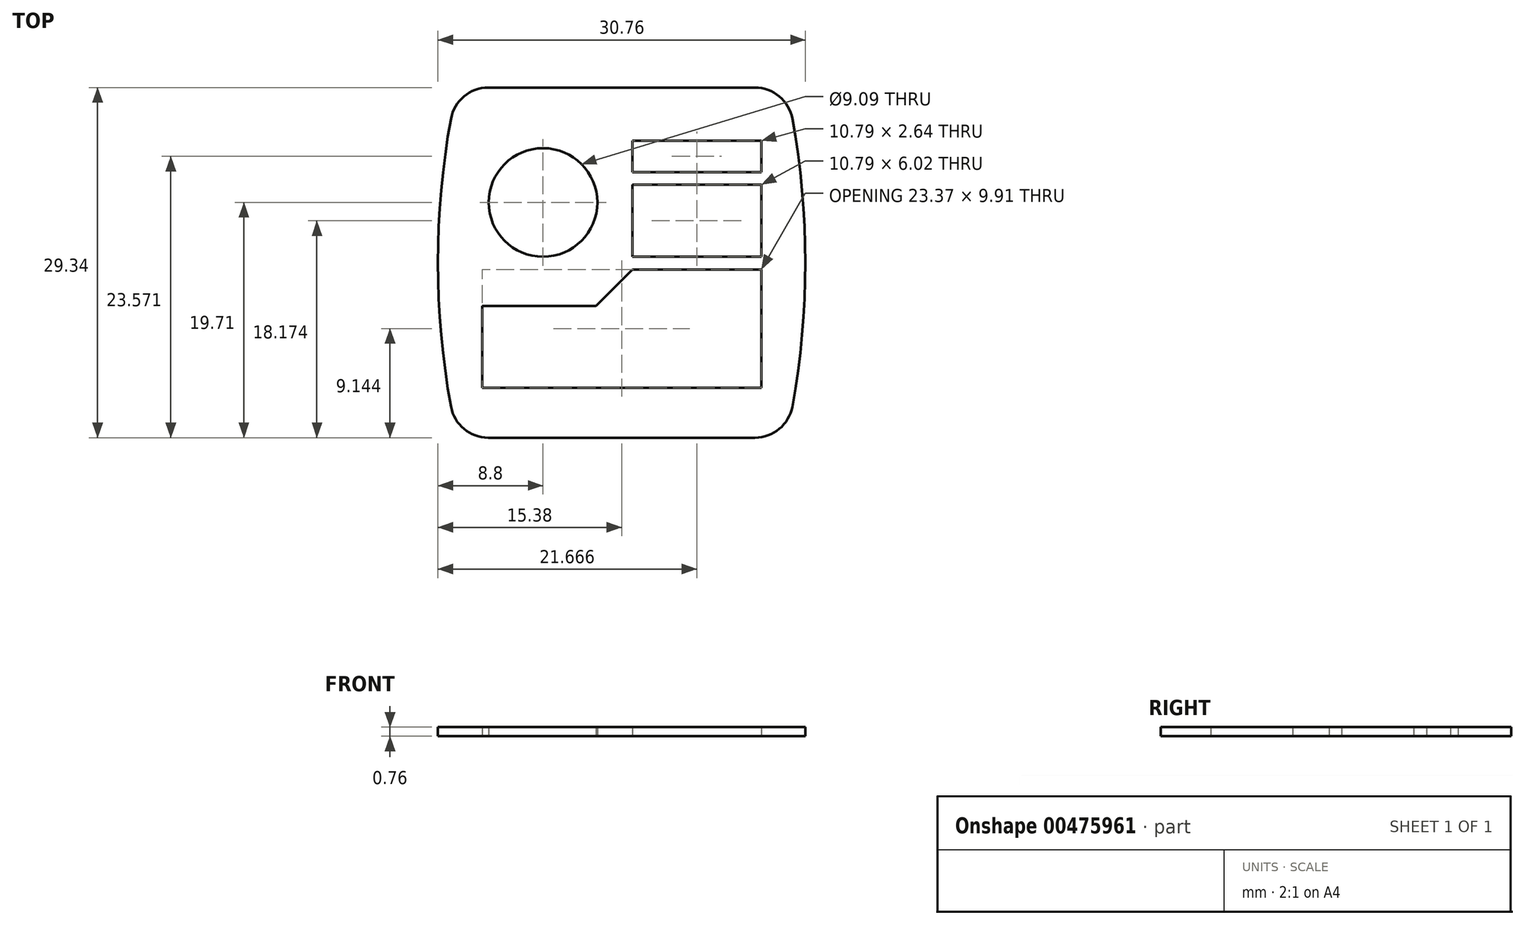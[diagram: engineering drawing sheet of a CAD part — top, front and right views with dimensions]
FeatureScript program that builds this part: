
annotation { "Feature Type Name" : "Feature", "Feature Type Description" : "" }
export const myFeature = defineFeature(function(context is Context, id is Id, definition is map)
    precondition{}
    {
        {
            var Q0;
            Q0=qCreatedBy(makeId("Top.planeOp"),FACE);
            var sketch = newSketch(context, id + "F0", { "sketchPlane" : qUnion([Q0])});
            skLineSegment(sketch, "E0.bottom", {"start": v(-11.16, 0) * mm, "end": v(11.16, 0) * mm});
            skLineSegment(sketch, "E0.top", {"start": v(-11.16, 29.34) * mm, "end": v(11.16, 29.34) * mm});
            skLineSegment(sketch, "E0.left", {"start": v(-13.76, 0) * mm, "end": v(-13.76, 29.34) * mm, "construction": true});
            skLineSegment(sketch, "E0.right", {"start": v(13.76, 0) * mm, "end": v(13.76, 29.34) * mm, "construction": true});
            skArc(sketch, "E1", {"start": v(-14.29, 26.73) * mm, "mid": v(-15.38, 14.67) * mm, "end": v(-14.29, 2.6) * mm});
            skArc(sketch, "E2.MirrorCS", {"start": v(14.29, 26.73) * mm, "mid": v(15.38, 14.67) * mm, "end": v(14.29, 2.6) * mm});
            skPoint(sketch, "E3", {"position": v(-15.38, 14.67) * mm});
            skPoint(sketch, "E4", {"position": v(15.38, 14.67) * mm});
            skCircle(sketch, "E5", {"center": v(-6.58, 19.71) * mm, "radius": 4.55 * mm});
            skLineSegment(sketch, "E6.bottom", {"start": v(0.89, 24.9) * mm, "end": v(11.68, 24.9) * mm});
            skLineSegment(sketch, "E6.top", {"start": v(0.89, 22.25) * mm, "end": v(11.68, 22.25) * mm});
            skLineSegment(sketch, "E6.left", {"start": v(0.89, 24.9) * mm, "end": v(0.89, 22.25) * mm});
            skLineSegment(sketch, "E6.right", {"start": v(11.68, 24.9) * mm, "end": v(11.68, 22.25) * mm});
            skLineSegment(sketch, "E7.bottom", {"start": v(0.89, 21.18) * mm, "end": v(11.68, 21.18) * mm});
            skLineSegment(sketch, "E7.top", {"start": v(0.89, 15.16) * mm, "end": v(11.68, 15.16) * mm});
            skLineSegment(sketch, "E7.left", {"start": v(0.89, 21.18) * mm, "end": v(0.89, 15.16) * mm});
            skLineSegment(sketch, "E7.right", {"start": v(11.68, 21.18) * mm, "end": v(11.68, 15.16) * mm});
            skLineSegment(sketch, "E8", {"start": v(11.68, 14.1) * mm, "end": v(11.68, 4.2) * mm});
            skLineSegment(sketch, "E9", {"start": v(11.68, 4.2) * mm, "end": v(-11.68, 4.2) * mm});
            skLineSegment(sketch, "E10", {"start": v(-11.68, 4.2) * mm, "end": v(-11.68, 11.05) * mm});
            skLineSegment(sketch, "E11", {"start": v(-11.68, 11.05) * mm, "end": v(-2.16, 11.05) * mm});
            skLineSegment(sketch, "E12", {"start": v(-2.16, 11.05) * mm, "end": v(0.89, 14.1) * mm});
            skLineSegment(sketch, "E13", {"start": v(0.89, 14.1) * mm, "end": v(11.68, 14.1) * mm});
            skLineSegment(sketch, "E14", {"start": v(-6.58, 19.71) * mm, "end": v(-6.58, 24.26) * mm, "construction": true});
            skLineSegment(sketch, "E15", {"start": v(-6.58, 19.71) * mm, "end": v(-11.13, 19.71) * mm, "construction": true});
            skLineSegment(sketch, "E16", {"start": v(-11.13, 19.71) * mm, "end": v(-15.2, 19.71) * mm, "construction": true});
            skPoint(sketch, "E17", {"position": v(0, 4.2) * mm});
            skPoint(sketch, "E18.visualSharp", {"position": v(13.76, 29.34) * mm});
            skArc(sketch, "E18.filletArc", {"start": v(14.29, 26.73) * mm, "mid": v(13.2, 28.6) * mm, "end": v(11.16, 29.34) * mm});
            skPoint(sketch, "E19.visualSharp", {"position": v(-13.76, 29.34) * mm});
            skArc(sketch, "E19.filletArc", {"start": v(-11.16, 29.34) * mm, "mid": v(-13.2, 28.6) * mm, "end": v(-14.29, 26.73) * mm});
            skPoint(sketch, "E20.visualSharp", {"position": v(-13.76, 0) * mm});
            skArc(sketch, "E20.filletArc", {"start": v(-14.29, 2.6) * mm, "mid": v(-13.2, 0.74) * mm, "end": v(-11.16, 0) * mm});
            skPoint(sketch, "E21.visualSharp", {"position": v(13.76, 0) * mm});
            skArc(sketch, "E21.filletArc", {"start": v(11.16, 0) * mm, "mid": v(13.2, 0.74) * mm, "end": v(14.29, 2.6) * mm});
            skSolve(sketch);
        }
        {
            var Q0;
            Q0=makeQuery(id+"F0.imprint","IMPRINT",FACE,{"disambiguationData":[TD([[makeQuery(id+"F0.imprint","IMPRINT",EDGE,{"derivedFrom":sQuery(id+"F0.wireOp",EDGE,"E0.bottom")}),1.0]])]});
            extrude(context, id + "F1", {"entities" : qUnion([Q0]), "depth" : 0.76 * mm});
        }
    });
